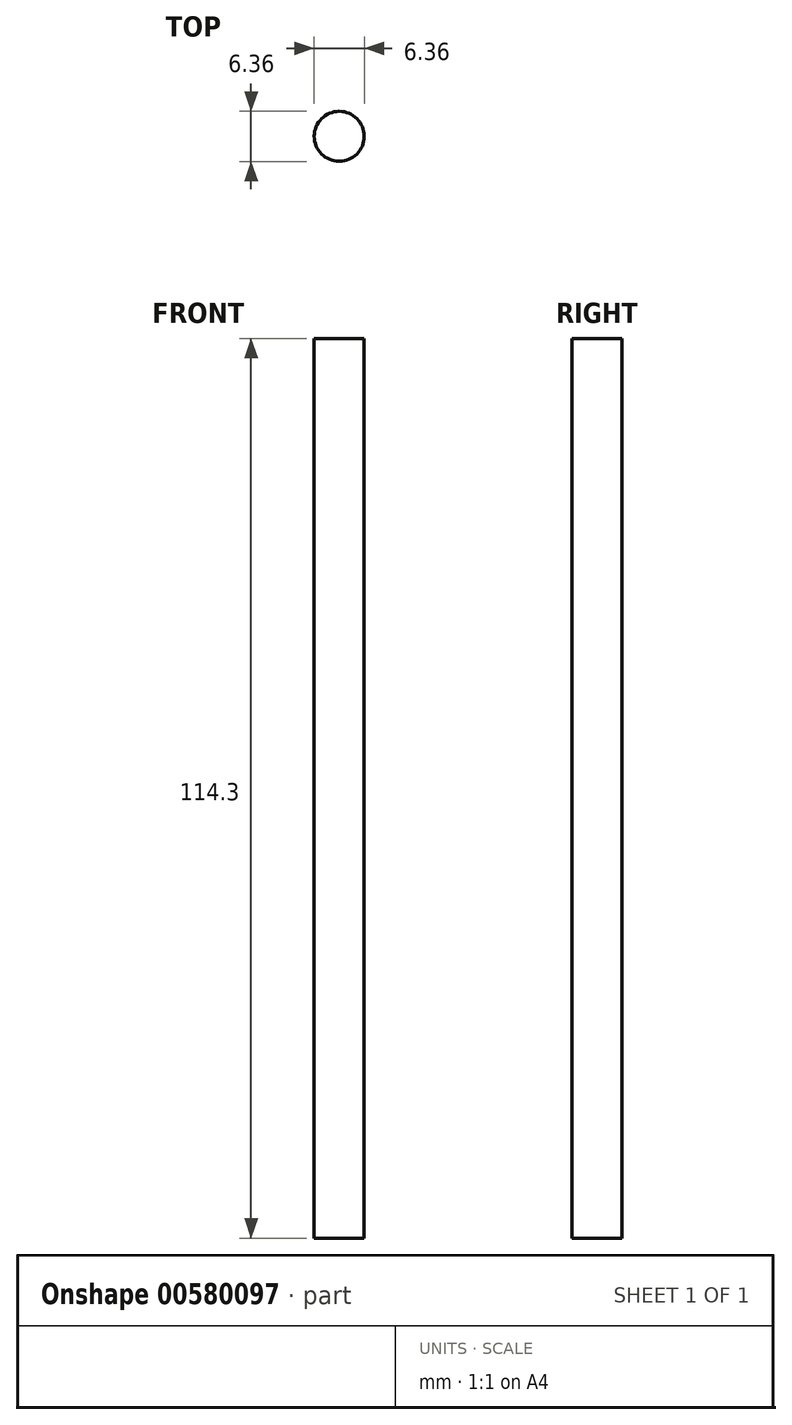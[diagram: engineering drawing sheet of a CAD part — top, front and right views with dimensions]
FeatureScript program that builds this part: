
annotation { "Feature Type Name" : "Feature", "Feature Type Description" : "" }
export const myFeature = defineFeature(function(context is Context, id is Id, definition is map)
    precondition{}
    {
        {
            var Q0;
            Q0=qCreatedBy(makeId("Top.planeOp"),FACE);
            var sketch = newSketch(context, id + "F0", { "sketchPlane" : qUnion([Q0])});
            skCircle(sketch, "E0", {"center": v(0, 0) * mm, "radius": 3.18 * mm});
            skSolve(sketch);
        }
        {
            var Q0;
            Q0=qSketchRegion(id+"F0",true);
            extrude(context, id + "F1", {"entities" : qUnion([Q0]), "depth" : 114.3 * mm});
        }
    });
